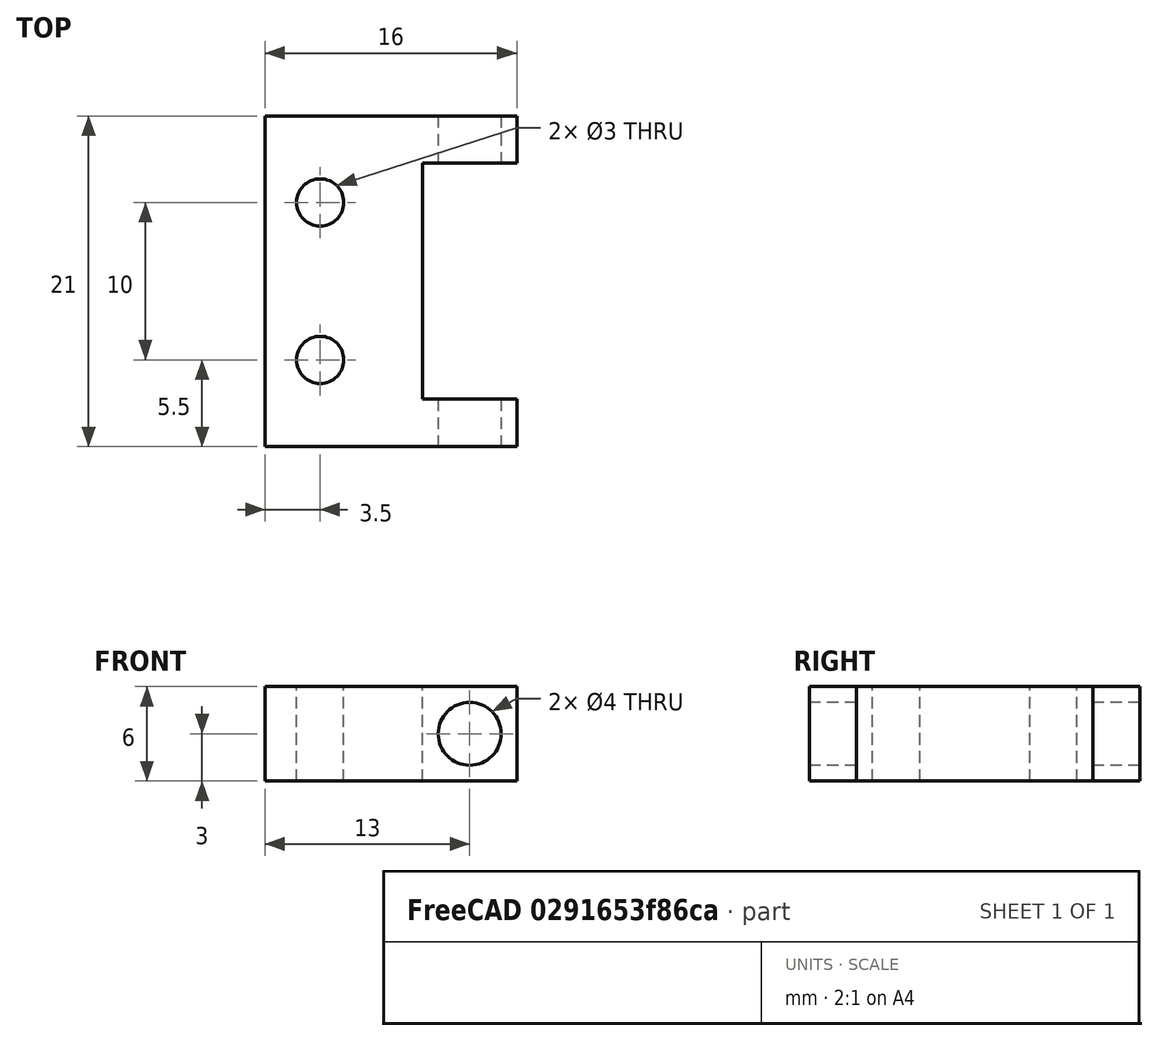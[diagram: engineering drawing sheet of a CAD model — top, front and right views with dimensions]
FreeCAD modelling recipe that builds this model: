
FCSTD DOCUMENT  (FreeCAD 0.14R3702 (Git))
Label: camera mount
License: All rights reserved
LicenseURL: http://en.wikipedia.org/wiki/All_rights_reserved
objects: Part::Box×3, Part::Cylinder×3, Part::Cut×3, Part::MultiFuse×1
note: 10 computed .brp shape members not serialized (recipe doc carries the construction recipe); baked Part::Feature solids carry a one-line shape summary decoded from their .brp

FEATURE [Part::Box] Box  label="Cube"
  Height = 6
  Length = 10
  Width = 15
FEATURE [Part::Cylinder] Cylinder
  Angle = 360
  Height = 10
  Placement = pos=(3.5,2.5,0) rot=(0,0,1;0rad)
  Radius = 1.5
FEATURE [Part::Cylinder] Cylinder001
  Angle = 360
  Height = 10
  Placement = pos=(3.5,12.5,0) rot=(0,0,1;0rad)
  Radius = 1.5
FEATURE [Part::Cylinder] Cylinder002
  Angle = 360
  Height = 30
  Placement = pos=(13,20,3) rot=(1,0,0;1.5708rad)
  Radius = 2
FEATURE [Part::Box] Box001  label="Cube001"
  Height = 6
  Length = 16
  Placement = pos=(0,-3,0) rot=(0,0,1;0rad)
  Width = 3
FEATURE [Part::Box] Box002  label="Cube002"
  Height = 6
  Length = 16
  Placement = pos=(0,15,0) rot=(0,0,1;0rad)
  Width = 3
FEATURE [Part::MultiFuse] Fusion
  Shapes = -> [Box001,Box,Box002]
FEATURE [Part::Cut] Cut
  Base = -> Fusion
  Tool = -> Cylinder002
FEATURE [Part::Cut] Cut001
  Base = -> Cut
  Tool = -> Cylinder
FEATURE [Part::Cut] Cut002
  Base = -> Cut001
  Tool = -> Cylinder001
